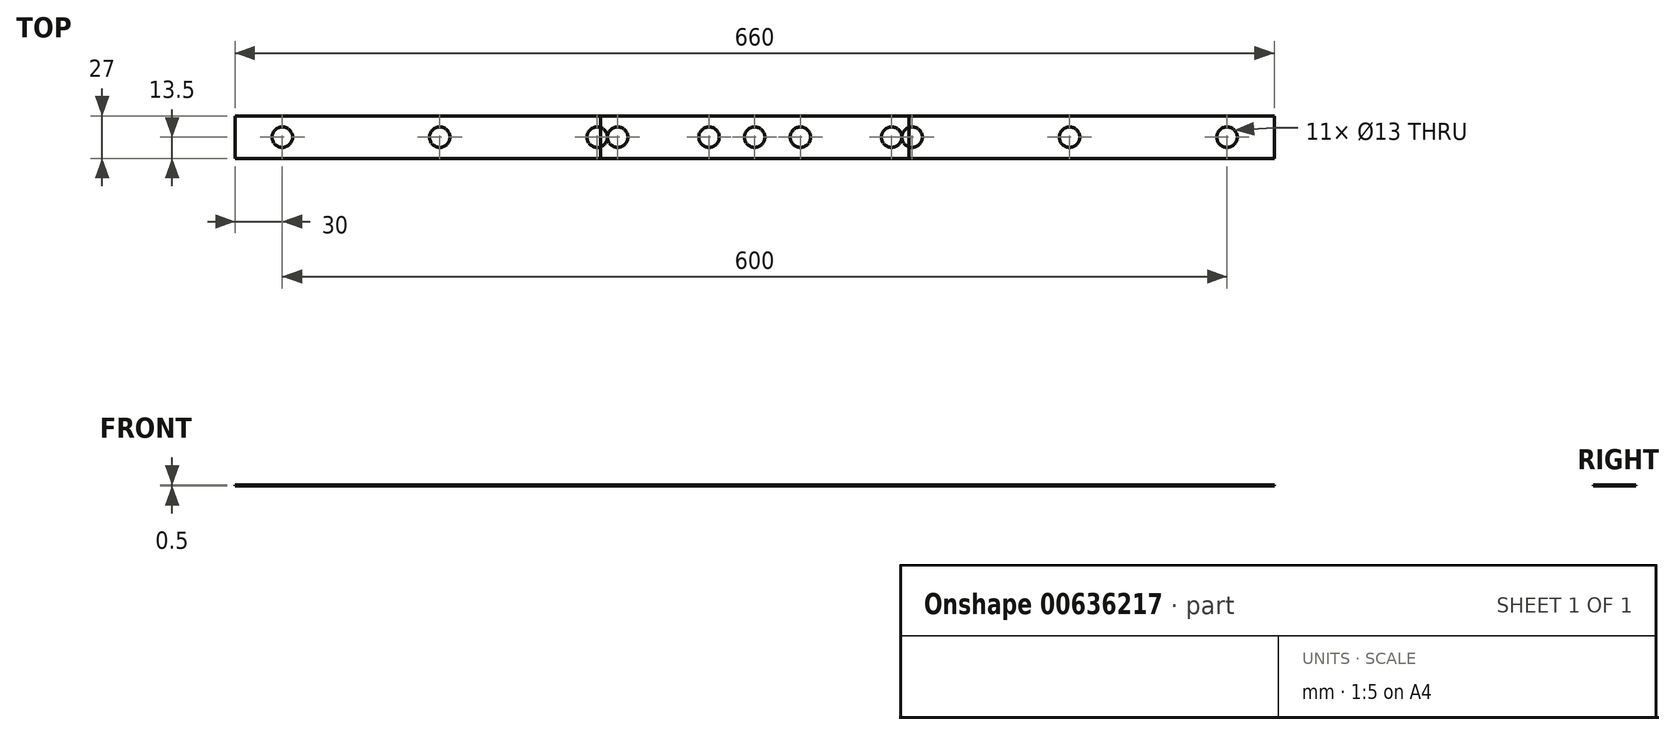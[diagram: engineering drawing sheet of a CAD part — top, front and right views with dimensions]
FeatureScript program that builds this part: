
annotation { "Feature Type Name" : "Feature", "Feature Type Description" : "" }
export const myFeature = defineFeature(function(context is Context, id is Id, definition is map)
    precondition{}
    {
        {
            var Q0;
            Q0=qCreatedBy(makeId("Top.planeOp"),FACE);
            var sketch = newSketch(context, id + "F0", { "sketchPlane" : qUnion([Q0])});
            skLineSegment(sketch, "E0.bottom", {"start": v(-98, 13.5) * mm, "end": v(98, 13.5) * mm});
            skLineSegment(sketch, "E0.top", {"start": v(-98, -13.5) * mm, "end": v(98, -13.5) * mm});
            skLineSegment(sketch, "E0.left", {"start": v(-98, 13.5) * mm, "end": v(-98, -13.5) * mm});
            skLineSegment(sketch, "E0.right", {"start": v(98, 13.5) * mm, "end": v(98, -13.5) * mm});
            skLineSegment(sketch, "E1", {"start": v(-114.98, 0) * mm, "end": v(117, 0) * mm, "construction": true});
            skCircle(sketch, "E2", {"center": v(-87, 0) * mm, "radius": 6.5 * mm});
            skCircle(sketch, "E3.1.0.0", {"center": v(-29, 0) * mm, "radius": 6.5 * mm});
            skCircle(sketch, "E3.2.0.0", {"center": v(29, 0) * mm, "radius": 6.5 * mm});
            skCircle(sketch, "E3.3.0.0", {"center": v(87, 0) * mm, "radius": 6.5 * mm});
            skLineSegment(sketch, "E3.direction1", {"start": v(-87, 0) * mm, "end": v(-29, 0) * mm, "construction": true});
            skSolve(sketch);
        }
        {
            var Q0;
            Q0=makeQuery(id+"F0.imprint","IMPRINT",FACE,{"disambiguationData":[TD([[makeQuery(id+"F0.imprint","IMPRINT",EDGE,{"derivedFrom":sQuery(id+"F0.wireOp",EDGE,"E0.bottom")}),-1.0]])]});
            extrude(context, id + "F1", {"entities" : qUnion([Q0]), "depth" : 0.5 * mm, "offsetDistance" : 25 * mm});
        }
        {
            var Q0;
            Q0=qCreatedBy(makeId("Top.planeOp"),FACE);
            var sketch = newSketch(context, id + "F2", { "sketchPlane" : qUnion([Q0])});
            skLineSegment(sketch, "E4.bottom", {"start": v(-330, 13.5) * mm, "end": v(330, 13.5) * mm});
            skLineSegment(sketch, "E4.top", {"start": v(-330, -13.5) * mm, "end": v(330, -13.5) * mm});
            skLineSegment(sketch, "E4.left", {"start": v(-330, 13.5) * mm, "end": v(-330, -13.5) * mm});
            skLineSegment(sketch, "E4.right", {"start": v(330, 13.5) * mm, "end": v(330, -13.5) * mm});
            skCircle(sketch, "E5", {"center": v(0, 0) * mm, "radius": 6.5 * mm});
            skCircle(sketch, "E6.1.0.0", {"center": v(100, 0) * mm, "radius": 6.5 * mm});
            skCircle(sketch, "E6.2.0.0", {"center": v(200, 0) * mm, "radius": 6.5 * mm});
            skCircle(sketch, "E6.3.0.0", {"center": v(300, 0) * mm, "radius": 6.5 * mm});
            skLineSegment(sketch, "E6.direction1", {"start": v(0, 0) * mm, "end": v(100, 0) * mm, "construction": true});
            skCircle(sketch, "E7.1.0.0", {"center": v(-100, 0) * mm, "radius": 6.5 * mm});
            skCircle(sketch, "E7.2.0.0", {"center": v(-200, 0) * mm, "radius": 6.5 * mm});
            skCircle(sketch, "E7.3.0.0", {"center": v(-300, 0) * mm, "radius": 6.5 * mm});
            skLineSegment(sketch, "E7.direction1", {"start": v(0, 0) * mm, "end": v(-100, 0) * mm, "construction": true});
            skSolve(sketch);
        }
        {
            var Q0;
            Q0=makeQuery(id+"F2.imprint","IMPRINT",FACE,{"disambiguationData":[TD([[makeQuery(id+"F2.imprint","IMPRINT",EDGE,{"derivedFrom":sQuery(id+"F2.wireOp",EDGE,"E4.bottom")}),-1.0]])]});
            extrude(context, id + "F3", {"entities" : qUnion([Q0]), "depth" : 0.5 * mm, "offsetDistance" : 25 * mm});
        }
    });
